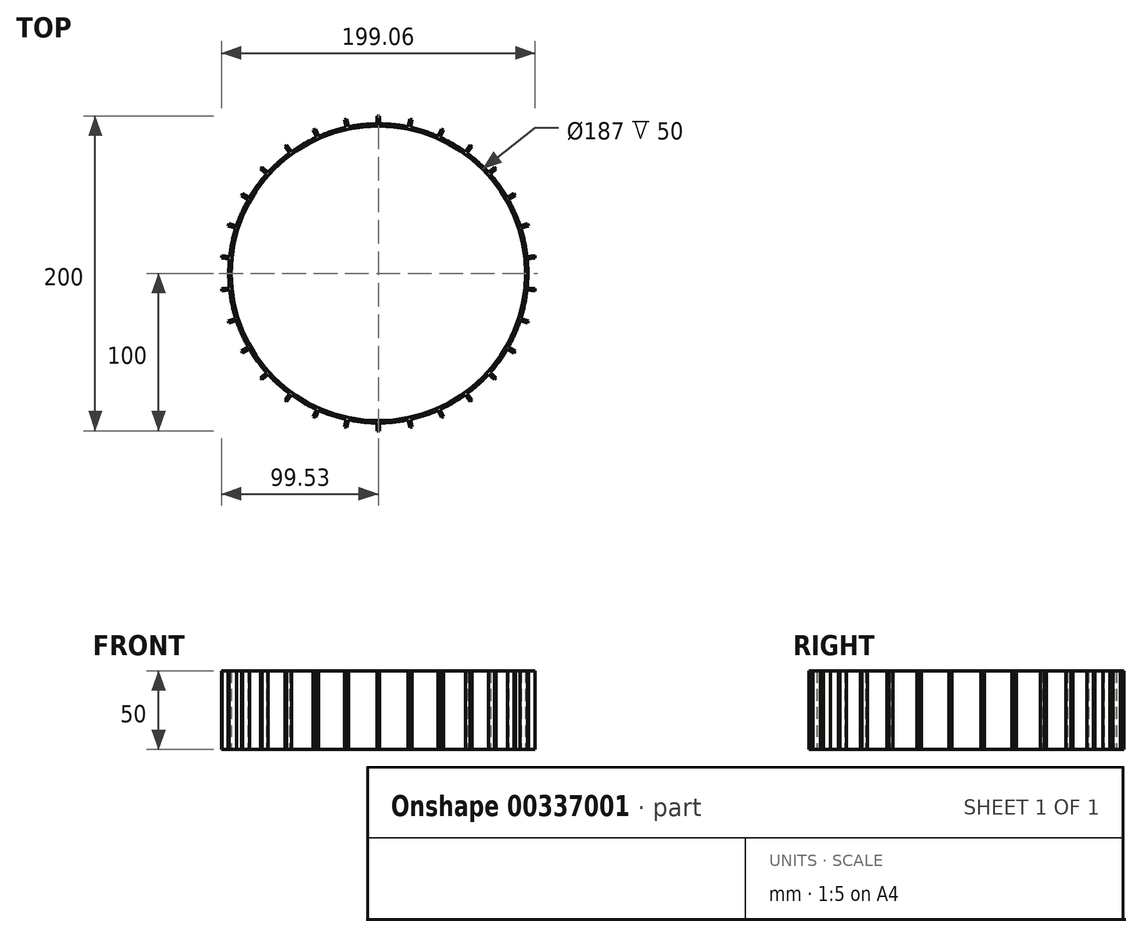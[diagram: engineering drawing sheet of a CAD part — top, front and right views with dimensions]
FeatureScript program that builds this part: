
annotation { "Feature Type Name" : "Feature", "Feature Type Description" : "" }
export const myFeature = defineFeature(function(context is Context, id is Id, definition is map)
    precondition{}
    {
        {
            var Q0;
            Q0=qCreatedBy(makeId("Top.planeOp"),FACE);
            var sketch = newSketch(context, id + "F0", { "sketchPlane" : qUnion([Q0])});
            skCircle(sketch, "E0", {"center": v(0, 0) * mm, "radius": 93.5 * mm});
            skCircle(sketch, "E1", {"center": v(0, 0) * mm, "radius": 95 * mm});
            skLineSegment(sketch, "E2.bottom", {"start": v(-0.75, 100) * mm, "end": v(0.75, 100) * mm});
            skLineSegment(sketch, "E2.top", {"start": v(-0.75, 95) * mm, "end": v(0.75, 95) * mm});
            skLineSegment(sketch, "E2.left", {"start": v(-0.75, 100) * mm, "end": v(-0.75, 95) * mm});
            skLineSegment(sketch, "E2.right", {"start": v(0.75, 100) * mm, "end": v(0.75, 95) * mm});
            skLineSegment(sketch, "E3.1.0", {"start": v(-21.52, 97.66) * mm, "end": v(-20.48, 92.77) * mm});
            skLineSegment(sketch, "E3.1.1", {"start": v(-21.52, 97.66) * mm, "end": v(-20.06, 97.97) * mm});
            skLineSegment(sketch, "E3.1.2", {"start": v(-20.06, 97.97) * mm, "end": v(-19.02, 93.08) * mm});
            skLineSegment(sketch, "E3.2.0", {"start": v(-41.36, 91.05) * mm, "end": v(-39.32, 86.48) * mm});
            skLineSegment(sketch, "E3.2.1", {"start": v(-41.36, 91.05) * mm, "end": v(-39.99, 91.66) * mm});
            skLineSegment(sketch, "E3.2.2", {"start": v(-39.99, 91.66) * mm, "end": v(-37.95, 87.09) * mm});
            skLineSegment(sketch, "E3.3.0", {"start": v(-59.38, 80.46) * mm, "end": v(-56.44, 76.41) * mm});
            skLineSegment(sketch, "E3.3.1", {"start": v(-59.38, 80.46) * mm, "end": v(-58.17, 81.34) * mm});
            skLineSegment(sketch, "E3.3.2", {"start": v(-58.17, 81.34) * mm, "end": v(-55.23, 77.3) * mm});
            skLineSegment(sketch, "E3.4.0", {"start": v(-74.81, 66.35) * mm, "end": v(-71.1, 63) * mm});
            skLineSegment(sketch, "E3.4.1", {"start": v(-74.81, 66.35) * mm, "end": v(-73.81, 67.47) * mm});
            skLineSegment(sketch, "E3.4.2", {"start": v(-73.81, 67.47) * mm, "end": v(-70.1, 64.12) * mm});
            skLineSegment(sketch, "E3.5.0", {"start": v(-86.97, 49.35) * mm, "end": v(-82.64, 46.85) * mm});
            skLineSegment(sketch, "E3.5.1", {"start": v(-86.97, 49.35) * mm, "end": v(-86.22, 50.65) * mm});
            skLineSegment(sketch, "E3.5.2", {"start": v(-86.22, 50.65) * mm, "end": v(-81.9, 48.15) * mm});
            skLineSegment(sketch, "E3.6.0", {"start": v(-95.33, 30.19) * mm, "end": v(-90.58, 28.64) * mm});
            skLineSegment(sketch, "E3.6.1", {"start": v(-95.33, 30.19) * mm, "end": v(-94.87, 31.61) * mm});
            skLineSegment(sketch, "E3.6.2", {"start": v(-94.87, 31.61) * mm, "end": v(-90.12, 30.07) * mm});
            skLineSegment(sketch, "E3.7.0", {"start": v(-99.53, 9.7) * mm, "end": v(-94.56, 9.18) * mm});
            skLineSegment(sketch, "E3.7.1", {"start": v(-99.53, 9.7) * mm, "end": v(-99.37, 11.2) * mm});
            skLineSegment(sketch, "E3.7.2", {"start": v(-99.37, 11.2) * mm, "end": v(-94.4, 10.68) * mm});
            skLineSegment(sketch, "E3.8.0", {"start": v(-99.37, -11.2) * mm, "end": v(-94.4, -10.68) * mm});
            skLineSegment(sketch, "E3.8.1", {"start": v(-99.37, -11.2) * mm, "end": v(-99.53, -9.7) * mm});
            skLineSegment(sketch, "E3.8.2", {"start": v(-99.53, -9.7) * mm, "end": v(-94.56, -9.18) * mm});
            skLineSegment(sketch, "E3.9.0", {"start": v(-94.87, -31.61) * mm, "end": v(-90.12, -30.07) * mm});
            skLineSegment(sketch, "E3.9.1", {"start": v(-94.87, -31.61) * mm, "end": v(-95.33, -30.19) * mm});
            skLineSegment(sketch, "E3.9.2", {"start": v(-95.33, -30.19) * mm, "end": v(-90.58, -28.64) * mm});
            skLineSegment(sketch, "E3.10.0", {"start": v(-86.22, -50.65) * mm, "end": v(-81.9, -48.15) * mm});
            skLineSegment(sketch, "E3.10.1", {"start": v(-86.22, -50.65) * mm, "end": v(-86.97, -49.35) * mm});
            skLineSegment(sketch, "E3.10.2", {"start": v(-86.97, -49.35) * mm, "end": v(-82.64, -46.85) * mm});
            skLineSegment(sketch, "E3.11.0", {"start": v(-73.81, -67.47) * mm, "end": v(-70.1, -64.12) * mm});
            skLineSegment(sketch, "E3.11.1", {"start": v(-73.81, -67.47) * mm, "end": v(-74.81, -66.35) * mm});
            skLineSegment(sketch, "E3.11.2", {"start": v(-74.81, -66.35) * mm, "end": v(-71.1, -63) * mm});
            skLineSegment(sketch, "E3.12.0", {"start": v(-58.17, -81.34) * mm, "end": v(-55.23, -77.3) * mm});
            skLineSegment(sketch, "E3.12.1", {"start": v(-58.17, -81.34) * mm, "end": v(-59.38, -80.46) * mm});
            skLineSegment(sketch, "E3.12.2", {"start": v(-59.38, -80.46) * mm, "end": v(-56.44, -76.41) * mm});
            skLineSegment(sketch, "E3.13.0", {"start": v(-39.99, -91.66) * mm, "end": v(-37.95, -87.09) * mm});
            skLineSegment(sketch, "E3.13.1", {"start": v(-39.99, -91.66) * mm, "end": v(-41.36, -91.05) * mm});
            skLineSegment(sketch, "E3.13.2", {"start": v(-41.36, -91.05) * mm, "end": v(-39.32, -86.48) * mm});
            skLineSegment(sketch, "E3.14.0", {"start": v(-20.06, -97.97) * mm, "end": v(-19.02, -93.08) * mm});
            skLineSegment(sketch, "E3.14.1", {"start": v(-20.06, -97.97) * mm, "end": v(-21.52, -97.66) * mm});
            skLineSegment(sketch, "E3.14.2", {"start": v(-21.52, -97.66) * mm, "end": v(-20.48, -92.77) * mm});
            skLineSegment(sketch, "E3.15.0", {"start": v(0.75, -100) * mm, "end": v(0.75, -95) * mm});
            skLineSegment(sketch, "E3.15.1", {"start": v(0.75, -100) * mm, "end": v(-0.75, -100) * mm});
            skLineSegment(sketch, "E3.15.2", {"start": v(-0.75, -100) * mm, "end": v(-0.75, -95) * mm});
            skLineSegment(sketch, "E3.16.0", {"start": v(21.52, -97.66) * mm, "end": v(20.48, -92.77) * mm});
            skLineSegment(sketch, "E3.16.1", {"start": v(21.52, -97.66) * mm, "end": v(20.06, -97.97) * mm});
            skLineSegment(sketch, "E3.16.2", {"start": v(20.06, -97.97) * mm, "end": v(19.02, -93.08) * mm});
            skLineSegment(sketch, "E3.17.0", {"start": v(41.36, -91.05) * mm, "end": v(39.32, -86.48) * mm});
            skLineSegment(sketch, "E3.17.1", {"start": v(41.36, -91.05) * mm, "end": v(39.99, -91.66) * mm});
            skLineSegment(sketch, "E3.17.2", {"start": v(39.99, -91.66) * mm, "end": v(37.95, -87.09) * mm});
            skLineSegment(sketch, "E3.18.0", {"start": v(59.38, -80.46) * mm, "end": v(56.44, -76.41) * mm});
            skLineSegment(sketch, "E3.18.1", {"start": v(59.38, -80.46) * mm, "end": v(58.17, -81.34) * mm});
            skLineSegment(sketch, "E3.18.2", {"start": v(58.17, -81.34) * mm, "end": v(55.23, -77.3) * mm});
            skLineSegment(sketch, "E3.19.0", {"start": v(74.81, -66.35) * mm, "end": v(71.1, -63) * mm});
            skLineSegment(sketch, "E3.19.1", {"start": v(74.81, -66.35) * mm, "end": v(73.81, -67.47) * mm});
            skLineSegment(sketch, "E3.19.2", {"start": v(73.81, -67.47) * mm, "end": v(70.1, -64.12) * mm});
            skLineSegment(sketch, "E3.20.0", {"start": v(86.97, -49.35) * mm, "end": v(82.64, -46.85) * mm});
            skLineSegment(sketch, "E3.20.1", {"start": v(86.97, -49.35) * mm, "end": v(86.22, -50.65) * mm});
            skLineSegment(sketch, "E3.20.2", {"start": v(86.22, -50.65) * mm, "end": v(81.9, -48.15) * mm});
            skLineSegment(sketch, "E3.21.0", {"start": v(95.33, -30.19) * mm, "end": v(90.58, -28.64) * mm});
            skLineSegment(sketch, "E3.21.1", {"start": v(95.33, -30.19) * mm, "end": v(94.87, -31.61) * mm});
            skLineSegment(sketch, "E3.21.2", {"start": v(94.87, -31.61) * mm, "end": v(90.12, -30.07) * mm});
            skLineSegment(sketch, "E3.22.0", {"start": v(99.53, -9.7) * mm, "end": v(94.56, -9.18) * mm});
            skLineSegment(sketch, "E3.22.1", {"start": v(99.53, -9.7) * mm, "end": v(99.37, -11.2) * mm});
            skLineSegment(sketch, "E3.22.2", {"start": v(99.37, -11.2) * mm, "end": v(94.4, -10.68) * mm});
            skLineSegment(sketch, "E3.23.0", {"start": v(99.37, 11.2) * mm, "end": v(94.4, 10.68) * mm});
            skLineSegment(sketch, "E3.23.1", {"start": v(99.37, 11.2) * mm, "end": v(99.53, 9.7) * mm});
            skLineSegment(sketch, "E3.23.2", {"start": v(99.53, 9.7) * mm, "end": v(94.56, 9.18) * mm});
            skLineSegment(sketch, "E3.24.0", {"start": v(94.87, 31.61) * mm, "end": v(90.12, 30.07) * mm});
            skLineSegment(sketch, "E3.24.1", {"start": v(94.87, 31.61) * mm, "end": v(95.33, 30.19) * mm});
            skLineSegment(sketch, "E3.24.2", {"start": v(95.33, 30.19) * mm, "end": v(90.58, 28.64) * mm});
            skLineSegment(sketch, "E3.25.0", {"start": v(86.22, 50.65) * mm, "end": v(81.9, 48.15) * mm});
            skLineSegment(sketch, "E3.25.1", {"start": v(86.22, 50.65) * mm, "end": v(86.97, 49.35) * mm});
            skLineSegment(sketch, "E3.25.2", {"start": v(86.97, 49.35) * mm, "end": v(82.64, 46.85) * mm});
            skLineSegment(sketch, "E3.26.0", {"start": v(73.81, 67.47) * mm, "end": v(70.1, 64.12) * mm});
            skLineSegment(sketch, "E3.26.1", {"start": v(73.81, 67.47) * mm, "end": v(74.81, 66.35) * mm});
            skLineSegment(sketch, "E3.26.2", {"start": v(74.81, 66.35) * mm, "end": v(71.1, 63) * mm});
            skLineSegment(sketch, "E3.27.0", {"start": v(58.17, 81.34) * mm, "end": v(55.23, 77.3) * mm});
            skLineSegment(sketch, "E3.27.1", {"start": v(58.17, 81.34) * mm, "end": v(59.38, 80.46) * mm});
            skLineSegment(sketch, "E3.27.2", {"start": v(59.38, 80.46) * mm, "end": v(56.44, 76.41) * mm});
            skLineSegment(sketch, "E3.28.0", {"start": v(39.99, 91.66) * mm, "end": v(37.95, 87.09) * mm});
            skLineSegment(sketch, "E3.28.1", {"start": v(39.99, 91.66) * mm, "end": v(41.36, 91.05) * mm});
            skLineSegment(sketch, "E3.28.2", {"start": v(41.36, 91.05) * mm, "end": v(39.32, 86.48) * mm});
            skLineSegment(sketch, "E3.29.0", {"start": v(20.06, 97.97) * mm, "end": v(19.02, 93.08) * mm});
            skLineSegment(sketch, "E3.29.1", {"start": v(20.06, 97.97) * mm, "end": v(21.52, 97.66) * mm});
            skLineSegment(sketch, "E3.29.2", {"start": v(21.52, 97.66) * mm, "end": v(20.48, 92.77) * mm});
            skSolve(sketch);
        }
        {
            var Q0;
            Q0=makeQuery(id+"F0.imprint","IMPRINT",FACE,{"disambiguationData":[TD([[makeQuery(id+"F0.imprint","IMPRINT",EDGE,{"derivedFrom":sQuery(id+"F0.wireOp",EDGE,"E0")}),-1.0]])]});
            var Q1;
            {var subQ1=sQuery(id+"F0.wireOp",EDGE,"E2.left");Q1=makeQuery(id+"F0.imprint","IMPRINT",FACE,{"disambiguationData":[TD([[makeQuery(id+"F0.imprint","IMPRINT",EDGE,{"derivedFrom":subQ1}),1.0]])]});}
            var Q2;
            {var subQ0=sQuery(id+"F0.wireOp",EDGE,"E3.29.0");Q2=makeQuery(id+"F0.imprint","IMPRINT",FACE,{"disambiguationData":[TD([[makeQuery(id+"F0.imprint","IMPRINT",EDGE,{"derivedFrom":subQ0}),1.0]])]});}
            var Q3;
            {var subQ0=sQuery(id+"F0.wireOp",EDGE,"E3.28.0");Q3=makeQuery(id+"F0.imprint","IMPRINT",FACE,{"disambiguationData":[TD([[makeQuery(id+"F0.imprint","IMPRINT",EDGE,{"derivedFrom":subQ0}),1.0]])]});}
            var Q4;
            {var subQ0=sQuery(id+"F0.wireOp",EDGE,"E3.27.0");Q4=makeQuery(id+"F0.imprint","IMPRINT",FACE,{"disambiguationData":[TD([[makeQuery(id+"F0.imprint","IMPRINT",EDGE,{"derivedFrom":subQ0}),1.0]])]});}
            var Q5;
            {var subQ0=sQuery(id+"F0.wireOp",EDGE,"E3.26.0");Q5=makeQuery(id+"F0.imprint","IMPRINT",FACE,{"disambiguationData":[TD([[makeQuery(id+"F0.imprint","IMPRINT",EDGE,{"derivedFrom":subQ0}),1.0]])]});}
            var Q6;
            {var subQ0=sQuery(id+"F0.wireOp",EDGE,"E3.25.0");Q6=makeQuery(id+"F0.imprint","IMPRINT",FACE,{"disambiguationData":[TD([[makeQuery(id+"F0.imprint","IMPRINT",EDGE,{"derivedFrom":subQ0}),1.0]])]});}
            var Q7;
            {var subQ0=sQuery(id+"F0.wireOp",EDGE,"E3.1.0");Q7=makeQuery(id+"F0.imprint","IMPRINT",FACE,{"disambiguationData":[TD([[makeQuery(id+"F0.imprint","IMPRINT",EDGE,{"derivedFrom":subQ0}),1.0]])]});}
            var Q8;
            {var subQ0=sQuery(id+"F0.wireOp",EDGE,"E3.2.0");Q8=makeQuery(id+"F0.imprint","IMPRINT",FACE,{"disambiguationData":[TD([[makeQuery(id+"F0.imprint","IMPRINT",EDGE,{"derivedFrom":subQ0}),1.0]])]});}
            var Q9;
            {var subQ0=sQuery(id+"F0.wireOp",EDGE,"E3.3.0");Q9=makeQuery(id+"F0.imprint","IMPRINT",FACE,{"disambiguationData":[TD([[makeQuery(id+"F0.imprint","IMPRINT",EDGE,{"derivedFrom":subQ0}),1.0]])]});}
            var Q10;
            {var subQ0=sQuery(id+"F0.wireOp",EDGE,"E3.4.0");Q10=makeQuery(id+"F0.imprint","IMPRINT",FACE,{"disambiguationData":[TD([[makeQuery(id+"F0.imprint","IMPRINT",EDGE,{"derivedFrom":subQ0}),1.0]])]});}
            var Q11;
            {var subQ0=sQuery(id+"F0.wireOp",EDGE,"E3.24.0");Q11=makeQuery(id+"F0.imprint","IMPRINT",FACE,{"disambiguationData":[TD([[makeQuery(id+"F0.imprint","IMPRINT",EDGE,{"derivedFrom":subQ0}),1.0]])]});}
            var Q12;
            {var subQ0=sQuery(id+"F0.wireOp",EDGE,"E3.23.0");Q12=makeQuery(id+"F0.imprint","IMPRINT",FACE,{"disambiguationData":[TD([[makeQuery(id+"F0.imprint","IMPRINT",EDGE,{"derivedFrom":subQ0}),1.0]])]});}
            var Q13;
            {var subQ0=sQuery(id+"F0.wireOp",EDGE,"E3.22.0");Q13=makeQuery(id+"F0.imprint","IMPRINT",FACE,{"disambiguationData":[TD([[makeQuery(id+"F0.imprint","IMPRINT",EDGE,{"derivedFrom":subQ0}),1.0]])]});}
            var Q14;
            {var subQ0=sQuery(id+"F0.wireOp",EDGE,"E3.21.0");Q14=makeQuery(id+"F0.imprint","IMPRINT",FACE,{"disambiguationData":[TD([[makeQuery(id+"F0.imprint","IMPRINT",EDGE,{"derivedFrom":subQ0}),1.0]])]});}
            var Q15;
            {var subQ0=sQuery(id+"F0.wireOp",EDGE,"E3.5.0");Q15=makeQuery(id+"F0.imprint","IMPRINT",FACE,{"disambiguationData":[TD([[makeQuery(id+"F0.imprint","IMPRINT",EDGE,{"derivedFrom":subQ0}),1.0]])]});}
            var Q16;
            {var subQ0=sQuery(id+"F0.wireOp",EDGE,"E3.6.0");Q16=makeQuery(id+"F0.imprint","IMPRINT",FACE,{"disambiguationData":[TD([[makeQuery(id+"F0.imprint","IMPRINT",EDGE,{"derivedFrom":subQ0}),1.0]])]});}
            var Q17;
            {var subQ0=sQuery(id+"F0.wireOp",EDGE,"E3.7.0");Q17=makeQuery(id+"F0.imprint","IMPRINT",FACE,{"disambiguationData":[TD([[makeQuery(id+"F0.imprint","IMPRINT",EDGE,{"derivedFrom":subQ0}),1.0]])]});}
            var Q18;
            {var subQ0=sQuery(id+"F0.wireOp",EDGE,"E3.8.0");Q18=makeQuery(id+"F0.imprint","IMPRINT",FACE,{"disambiguationData":[TD([[makeQuery(id+"F0.imprint","IMPRINT",EDGE,{"derivedFrom":subQ0}),1.0]])]});}
            var Q19;
            {var subQ0=sQuery(id+"F0.wireOp",EDGE,"E3.9.0");Q19=makeQuery(id+"F0.imprint","IMPRINT",FACE,{"disambiguationData":[TD([[makeQuery(id+"F0.imprint","IMPRINT",EDGE,{"derivedFrom":subQ0}),1.0]])]});}
            var Q20;
            {var subQ0=sQuery(id+"F0.wireOp",EDGE,"E3.10.0");Q20=makeQuery(id+"F0.imprint","IMPRINT",FACE,{"disambiguationData":[TD([[makeQuery(id+"F0.imprint","IMPRINT",EDGE,{"derivedFrom":subQ0}),1.0]])]});}
            var Q21;
            {var subQ0=sQuery(id+"F0.wireOp",EDGE,"E3.20.0");Q21=makeQuery(id+"F0.imprint","IMPRINT",FACE,{"disambiguationData":[TD([[makeQuery(id+"F0.imprint","IMPRINT",EDGE,{"derivedFrom":subQ0}),1.0]])]});}
            var Q22;
            {var subQ0=sQuery(id+"F0.wireOp",EDGE,"E3.11.0");Q22=makeQuery(id+"F0.imprint","IMPRINT",FACE,{"disambiguationData":[TD([[makeQuery(id+"F0.imprint","IMPRINT",EDGE,{"derivedFrom":subQ0}),1.0]])]});}
            var Q23;
            {var subQ0=sQuery(id+"F0.wireOp",EDGE,"E3.12.0");Q23=makeQuery(id+"F0.imprint","IMPRINT",FACE,{"disambiguationData":[TD([[makeQuery(id+"F0.imprint","IMPRINT",EDGE,{"derivedFrom":subQ0}),1.0]])]});}
            var Q24;
            {var subQ0=sQuery(id+"F0.wireOp",EDGE,"E3.13.0");Q24=makeQuery(id+"F0.imprint","IMPRINT",FACE,{"disambiguationData":[TD([[makeQuery(id+"F0.imprint","IMPRINT",EDGE,{"derivedFrom":subQ0}),1.0]])]});}
            var Q25;
            {var subQ0=sQuery(id+"F0.wireOp",EDGE,"E3.14.0");Q25=makeQuery(id+"F0.imprint","IMPRINT",FACE,{"disambiguationData":[TD([[makeQuery(id+"F0.imprint","IMPRINT",EDGE,{"derivedFrom":subQ0}),1.0]])]});}
            var Q26;
            {var subQ0=sQuery(id+"F0.wireOp",EDGE,"E3.15.0");Q26=makeQuery(id+"F0.imprint","IMPRINT",FACE,{"disambiguationData":[TD([[makeQuery(id+"F0.imprint","IMPRINT",EDGE,{"derivedFrom":subQ0}),1.0]])]});}
            var Q27;
            {var subQ0=sQuery(id+"F0.wireOp",EDGE,"E3.16.0");Q27=makeQuery(id+"F0.imprint","IMPRINT",FACE,{"disambiguationData":[TD([[makeQuery(id+"F0.imprint","IMPRINT",EDGE,{"derivedFrom":subQ0}),1.0]])]});}
            var Q28;
            {var subQ0=sQuery(id+"F0.wireOp",EDGE,"E3.17.0");Q28=makeQuery(id+"F0.imprint","IMPRINT",FACE,{"disambiguationData":[TD([[makeQuery(id+"F0.imprint","IMPRINT",EDGE,{"derivedFrom":subQ0}),1.0]])]});}
            var Q29;
            {var subQ0=sQuery(id+"F0.wireOp",EDGE,"E3.18.0");Q29=makeQuery(id+"F0.imprint","IMPRINT",FACE,{"disambiguationData":[TD([[makeQuery(id+"F0.imprint","IMPRINT",EDGE,{"derivedFrom":subQ0}),1.0]])]});}
            var Q30;
            {var subQ0=sQuery(id+"F0.wireOp",EDGE,"E3.19.0");Q30=makeQuery(id+"F0.imprint","IMPRINT",FACE,{"disambiguationData":[TD([[makeQuery(id+"F0.imprint","IMPRINT",EDGE,{"derivedFrom":subQ0}),1.0]])]});}
            extrude(context, id + "F1", {"entities" : qUnion([Q0, Q1, Q2, Q3, Q4, Q5, Q6, Q7, Q8, Q9, Q10, Q11, Q12, Q13, Q14, Q15, Q16, Q17, Q18, Q19, Q20, Q21, Q22, Q23, Q24, Q25, Q26, Q27, Q28, Q29, Q30]), "depth" : 50 * mm});
        }
        {
            var Q0;
            Q0=qCreatedBy(makeId("Top.planeOp"),FACE);
            cPlane(context, id + "F2", {"entities" : qUnion([Q0]), "cplaneType" : CPlaneType.OFFSET, "offset" : 25 * mm, "width" : 150 * mm, "height" : 150 * mm});
        }
    });
